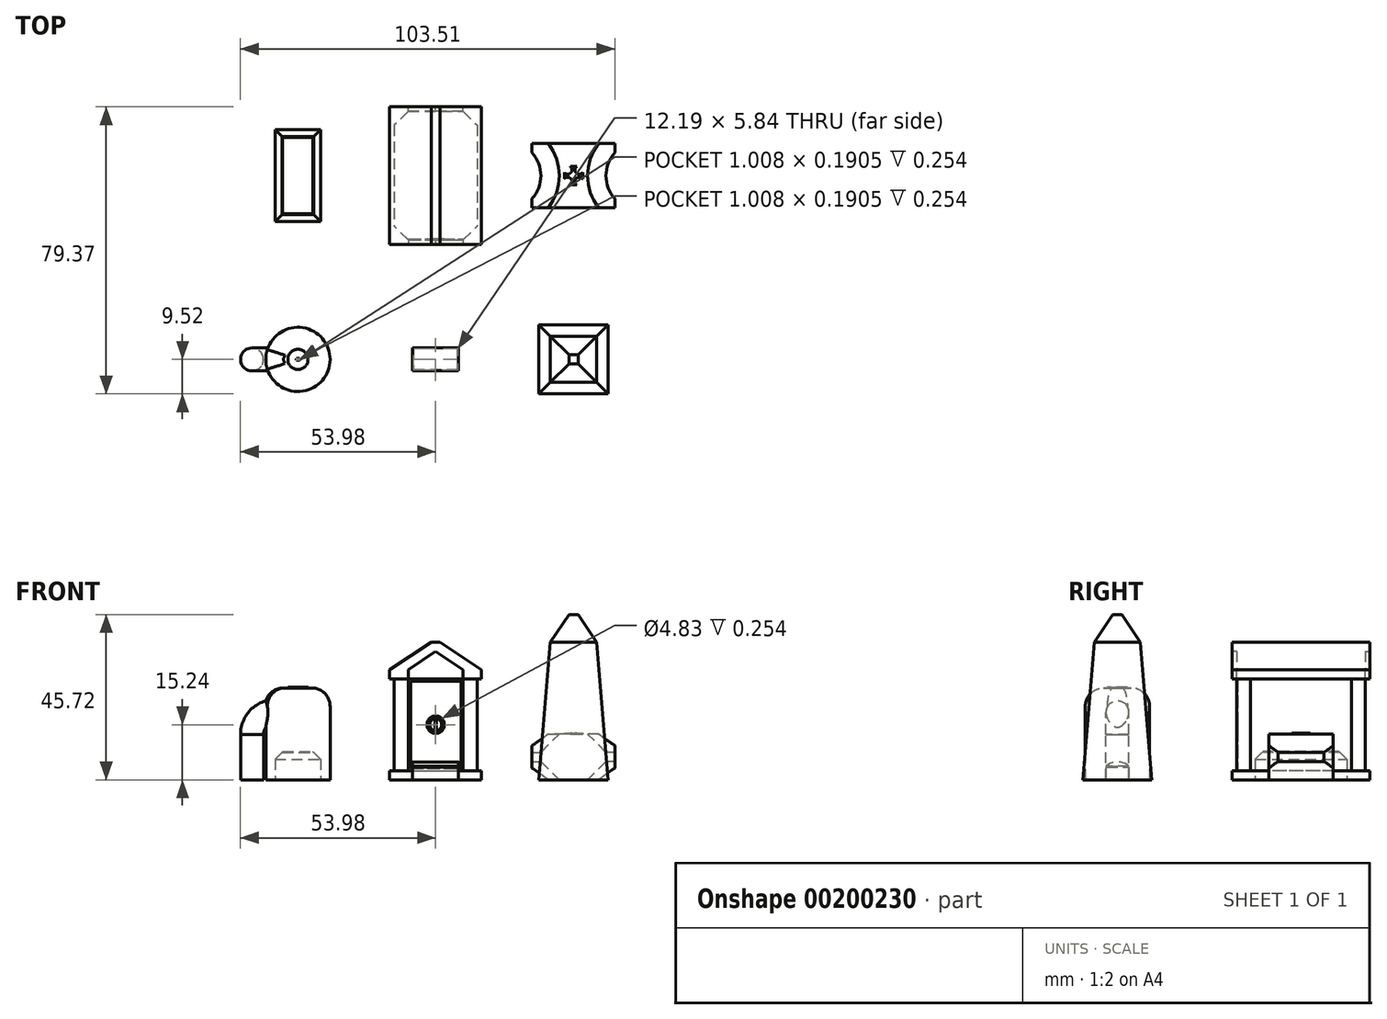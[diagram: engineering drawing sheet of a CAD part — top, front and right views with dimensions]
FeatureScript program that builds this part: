
annotation { "Feature Type Name" : "Feature", "Feature Type Description" : "" }
export const myFeature = defineFeature(function(context is Context, id is Id, definition is map)
    precondition{}
    {
        {
            var Q0;
            Q0=qCreatedBy(makeId("Top.planeOp"),FACE);
            var sketch = newSketch(context, id + "F0", { "sketchPlane" : qUnion([Q0])});
            skLineSegment(sketch, "E0", {"start": v(0, 0) * mm, "end": v(-38.1, 0) * mm, "construction": true});
            skLineSegment(sketch, "E1", {"start": v(0, 0) * mm, "end": v(38.1, 0) * mm, "construction": true});
            skLineSegment(sketch, "E2", {"start": v(0, 0) * mm, "end": v(0, 25.4) * mm, "construction": true});
            skLineSegment(sketch, "E3", {"start": v(-38.1, 0) * mm, "end": v(-38.1, 25.4) * mm, "construction": true});
            skLineSegment(sketch, "E4", {"start": v(38.1, 0) * mm, "end": v(38.1, 25.4) * mm, "construction": true});
            skLineSegment(sketch, "E5", {"start": v(-38.1, 0) * mm, "end": v(-38.1, -25.4) * mm, "construction": true});
            skLineSegment(sketch, "E6", {"start": v(0, 0) * mm, "end": v(0, -25.4) * mm, "construction": true});
            skLineSegment(sketch, "E7", {"start": v(38.1, 0) * mm, "end": v(38.1, -25.4) * mm, "construction": true});
            skSolve(sketch);
        }
        {
            var Q0;
            Q0=qCreatedBy(makeId("Top.planeOp"),FACE);
            var sketch = newSketch(context, id + "F1", { "sketchPlane" : qUnion([Q0])});
            skLineSegment(sketch, "E8.bottom", {"start": v(-44.45, 38.1) * mm, "end": v(-31.75, 38.1) * mm});
            skLineSegment(sketch, "E8.top", {"start": v(-44.45, 12.7) * mm, "end": v(-31.75, 12.7) * mm});
            skLineSegment(sketch, "E8.left", {"start": v(-44.45, 38.1) * mm, "end": v(-44.45, 12.7) * mm});
            skLineSegment(sketch, "E8.right", {"start": v(-31.75, 38.1) * mm, "end": v(-31.75, 12.7) * mm});
            skPoint(sketch, "E8.middle", {"position": v(-38.1, 25.4) * mm});
            skSolve(sketch);
        }
        {
            var Q0;
            Q0 = qSketchRegion(id + "F1", true);
            extrude(context, id + "F2", {"entities" : qUnion([Q0]), "depth" : 7.62 * mm});
        }
        {
            var Q0;
            Q0=makeQuery(id+"F2.opExtrude","CAP_FACE",FACE,{"disambiguationData":[OSD([sQuery(id+"F1.wireOp",EDGE,"E8.bottom"),sQuery(id+"F1.wireOp",EDGE,"E8.top"),sQuery(id+"F1.wireOp",EDGE,"E8.left"),sQuery(id+"F1.wireOp",EDGE,"E8.right")])],"isStart":false});
            chamfer(context, id + "F3", {"entities" : qUnion([Q0]), "width" : 1.9 * mm, "tangentPropagation" : true});
        }
        {
            var Q0;
            Q0=makeQuery(id+"F2.opExtrude","CAP_FACE",FACE,{"disambiguationData":[OSD([sQuery(id+"F1.wireOp",EDGE,"E8.bottom"),sQuery(id+"F1.wireOp",EDGE,"E8.top"),sQuery(id+"F1.wireOp",EDGE,"E8.left"),sQuery(id+"F1.wireOp",EDGE,"E8.right")])],"isStart":false});
            var sketch = newSketch(context, id + "F4", { "sketchPlane" : qUnion([Q0])});
            skLineSegment(sketch, "E9", {"start": v(-33.65, 25.4) * mm, "end": v(-38.1, 25.4) * mm, "construction": true});
            skPoint(sketch, "E9.endSnap0", {"position": v(-42.55, 25.4) * mm});
            skLineSegment(sketch, "E10.bottom", {"start": v(-42.3, 35.94) * mm, "end": v(-33.9, 35.94) * mm});
            skLineSegment(sketch, "E10.top", {"start": v(-42.3, 14.86) * mm, "end": v(-33.9, 14.86) * mm});
            skLineSegment(sketch, "E10.left", {"start": v(-42.3, 35.94) * mm, "end": v(-42.3, 14.86) * mm});
            skLineSegment(sketch, "E10.right", {"start": v(-33.9, 35.94) * mm, "end": v(-33.9, 14.86) * mm});
            skPoint(sketch, "E10.middle", {"position": v(-38.1, 25.4) * mm});
            skSolve(sketch);
        }
        {
            var Q0;
            Q0 = qSketchRegion(id + "F4", true);
            extrude(context, id + "F5", {"entities" : qUnion([Q0]), "operationType" : NewBodyOperationType.ADD, "depth" : 0.25 * mm});
        }
        {
            var Q0;
            Q0=qCreatedBy(makeId("Top.planeOp"),FACE);
            var sketch = newSketch(context, id + "F6", { "sketchPlane" : qUnion([Q0])});
            skLineSegment(sketch, "E11.bottom", {"start": v(-12.7, 44.45) * mm, "end": v(12.7, 44.45) * mm});
            skLineSegment(sketch, "E11.top", {"start": v(-12.7, 6.35) * mm, "end": v(12.7, 6.35) * mm});
            skLineSegment(sketch, "E11.left", {"start": v(-12.7, 44.45) * mm, "end": v(-12.7, 6.35) * mm});
            skLineSegment(sketch, "E11.right", {"start": v(12.7, 44.45) * mm, "end": v(12.7, 6.35) * mm});
            skPoint(sketch, "E11.middle", {"position": v(0, 25.4) * mm});
            skSolve(sketch);
        }
        {
            var Q0;
            Q0 = qSketchRegion(id + "F6", true);
            extrude(context, id + "F7", {"entities" : qUnion([Q0]), "depth" : 2.54 * mm});
        }
        {
            var Q0;
            Q0=makeQuery(id+"F7.opExtrude","CAP_FACE",FACE,{"disambiguationData":[OSD([sQuery(id+"F6.wireOp",EDGE,"E11.bottom"),sQuery(id+"F6.wireOp",EDGE,"E11.top"),sQuery(id+"F6.wireOp",EDGE,"E11.left"),sQuery(id+"F6.wireOp",EDGE,"E11.right")])],"isStart":false});
            var sketch = newSketch(context, id + "F8", { "sketchPlane" : qUnion([Q0])});
            skLineSegment(sketch, "E12.bottom", {"start": v(-11.43, 43.18) * mm, "end": v(11.43, 43.18) * mm});
            skLineSegment(sketch, "E12.top", {"start": v(-11.43, 7.62) * mm, "end": v(11.43, 7.62) * mm});
            skLineSegment(sketch, "E12.left", {"start": v(-11.43, 43.18) * mm, "end": v(-11.43, 7.62) * mm});
            skLineSegment(sketch, "E12.right", {"start": v(11.43, 43.18) * mm, "end": v(11.43, 7.62) * mm});
            skPoint(sketch, "E12.middle", {"position": v(0, 25.4) * mm});
            skSolve(sketch);
        }
        {
            var Q0;
            Q0 = qSketchRegion(id + "F8", true);
            extrude(context, id + "F9", {"entities" : qUnion([Q0]), "operationType" : NewBodyOperationType.ADD, "depth" : 25.4 * mm});
        }
        {
            var Q0;
            Q0=makeQuery(id+"F9.opExtrude","SWEPT_EDGE",EDGE,{"disambiguationData":[OSD([sQuery(id+"F8.wireOp",EDGE,"E12.top"),sQuery(id+"F8.wireOp",EDGE,"E12.left")])]});
            var Q1;
            Q1=makeQuery(id+"F9.opExtrude","SWEPT_EDGE",EDGE,{"disambiguationData":[OSD([sQuery(id+"F8.wireOp",EDGE,"E12.top"),sQuery(id+"F8.wireOp",EDGE,"E12.right")])]});
            var Q2;
            Q2=makeQuery(id+"F9.opExtrude","SWEPT_EDGE",EDGE,{"disambiguationData":[OSD([sQuery(id+"F8.wireOp",EDGE,"E12.bottom"),sQuery(id+"F8.wireOp",EDGE,"E12.right")])]});
            var Q3;
            Q3=makeQuery(id+"F9.opExtrude","SWEPT_EDGE",EDGE,{"disambiguationData":[OSD([sQuery(id+"F8.wireOp",EDGE,"E12.bottom"),sQuery(id+"F8.wireOp",EDGE,"E12.left")])]});
            chamfer(context, id + "F10", {"entities" : qUnion([Q0, Q1, Q2, Q3]), "width" : 3.8 * mm, "tangentPropagation" : true});
        }
        {
            var Q0;
            Q0=makeQuery(id+"F9.opExtrude","CAP_FACE",FACE,{"disambiguationData":[OSD([sQuery(id+"F8.wireOp",EDGE,"E12.bottom"),sQuery(id+"F8.wireOp",EDGE,"E12.top"),sQuery(id+"F8.wireOp",EDGE,"E12.left"),sQuery(id+"F8.wireOp",EDGE,"E12.right")])],"isStart":false});
            var sketch = newSketch(context, id + "F11", { "sketchPlane" : qUnion([Q0])});
            skLineSegment(sketch, "E13.bottom", {"start": v(-12.7, 44.45) * mm, "end": v(12.7, 44.45) * mm});
            skLineSegment(sketch, "E13.top", {"start": v(-12.7, 6.35) * mm, "end": v(12.7, 6.35) * mm});
            skLineSegment(sketch, "E13.left", {"start": v(-12.7, 44.45) * mm, "end": v(-12.7, 6.35) * mm});
            skLineSegment(sketch, "E13.right", {"start": v(12.7, 44.45) * mm, "end": v(12.7, 6.35) * mm});
            skPoint(sketch, "E13.middle", {"position": v(0, 25.4) * mm});
            skSolve(sketch);
        }
        {
            var Q0;
            {var subQ3=sQuery(id+"F8.wireOp",EDGE,"E12.bottom");Q0=makeQuery(id+"F11.imprint","IMPRINT",FACE,{"disambiguationData":[TD([[makeQuery(id+"F11.imprint","IMPRINT",EDGE,{"derivedFrom":makeQuery(id+"F9.opExtrude","CAP_EDGE",EDGE,{"disambiguationData":[OSD([subQ3])],"isStart":false})}),-1.0]])]});}
            cPlane(context, id + "F12", {"entities" : qUnion([Q0]), "cplaneType" : CPlaneType.OFFSET, "offset" : 10.16 * mm, "width" : 152.4 * mm, "height" : 152.4 * mm});
        }
        {
            var Q0;
            Q0=qCreatedBy(id+"F12.planeOp",FACE);
            var sketch = newSketch(context, id + "F13", { "sketchPlane" : qUnion([Q0])});
            skLineSegment(sketch, "E14.bottom", {"start": v(-1.27, 44.45) * mm, "end": v(1.27, 44.45) * mm});
            skLineSegment(sketch, "E14.top", {"start": v(-1.27, 6.35) * mm, "end": v(1.27, 6.35) * mm});
            skLineSegment(sketch, "E14.left", {"start": v(-1.27, 44.45) * mm, "end": v(-1.27, 6.35) * mm});
            skLineSegment(sketch, "E14.right", {"start": v(1.27, 44.45) * mm, "end": v(1.27, 6.35) * mm});
            skPoint(sketch, "E14.middle", {"position": v(0, 25.4) * mm});
            skSolve(sketch);
        }
        {
            var Q0;
            Q0=qCreatedBy(makeId("Front.planeOp"),FACE);
            cPlane(context, id + "F14", {"entities" : qUnion([Q0]), "cplaneType" : CPlaneType.OFFSET, "offset" : 6.35 * mm, "oppositeDirection" : true, "width" : 152.4 * mm, "height" : 152.4 * mm});
        }
        {
            var Q0;
            Q0=qCreatedBy(id+"F14.planeOp",FACE);
            var sketch = newSketch(context, id + "F15", { "sketchPlane" : qUnion([Q0])});
            skLineSegment(sketch, "E15", {"start": v(-12.7, 27.94) * mm, "end": v(-12.7, 30.48) * mm});
            skLineSegment(sketch, "E16", {"start": v(-12.7, 30.48) * mm, "end": v(-1.27, 38.1) * mm});
            skLineSegment(sketch, "E17", {"start": v(-1.27, 38.1) * mm, "end": v(1.27, 38.1) * mm});
            skLineSegment(sketch, "E18", {"start": v(1.27, 38.1) * mm, "end": v(12.7, 30.48) * mm});
            skLineSegment(sketch, "E19", {"start": v(12.7, 30.48) * mm, "end": v(12.7, 27.94) * mm});
            skLineSegment(sketch, "E20", {"start": v(-12.7, 27.94) * mm, "end": v(12.7, 27.94) * mm});
            skSolve(sketch);
        }
        {
            var Q0;
            Q0 = qSketchRegion(id + "F15", true);
            extrude(context, id + "F16", {"entities" : qUnion([Q0]), "oppositeDirection" : true, "depth" : 38.1 * mm});
        }
        {
            var Q0;
            Q0=makeQuery(id+"F16.opExtrude","CAP_FACE",FACE,{"disambiguationData":[OSD([sQuery(id+"F15.wireOp",EDGE,"E15"),sQuery(id+"F15.wireOp",EDGE,"E16"),sQuery(id+"F15.wireOp",EDGE,"E17"),sQuery(id+"F15.wireOp",EDGE,"E18"),sQuery(id+"F15.wireOp",EDGE,"E19"),sQuery(id+"F15.wireOp",EDGE,"E20")])],"isStart":true});
            var sketch = newSketch(context, id + "F17", { "sketchPlane" : qUnion([Q0])});
            skLineSegment(sketch, "E21", {"start": v(-7.62, 27.94) * mm, "end": v(-7.62, 30.48) * mm});
            skLineSegment(sketch, "E22", {"start": v(-7.62, 30.48) * mm, "end": v(0, 35.56) * mm});
            skLineSegment(sketch, "E23", {"start": v(0, 35.56) * mm, "end": v(7.62, 30.48) * mm});
            skLineSegment(sketch, "E24", {"start": v(7.62, 30.48) * mm, "end": v(7.62, 27.94) * mm});
            skLineSegment(sketch, "E25", {"start": v(-7.62, 27.94) * mm, "end": v(7.62, 27.94) * mm});
            skSolve(sketch);
        }
        {
            var Q0;
            Q0 = qSketchRegion(id + "F17", true);
            extrude(context, id + "F18", {"entities" : qUnion([Q0]), "operationType" : NewBodyOperationType.REMOVE, "oppositeDirection" : true, "depth" : 1.27 * mm});
        }
        {
            var Q0;
            Q0=makeQuery(id+"F16.opExtrude","CAP_FACE",FACE,{"disambiguationData":[OSD([sQuery(id+"F15.wireOp",EDGE,"E15"),sQuery(id+"F15.wireOp",EDGE,"E16"),sQuery(id+"F15.wireOp",EDGE,"E17"),sQuery(id+"F15.wireOp",EDGE,"E18"),sQuery(id+"F15.wireOp",EDGE,"E19"),sQuery(id+"F15.wireOp",EDGE,"E20")])],"isStart":false});
            var sketch = newSketch(context, id + "F19", { "sketchPlane" : qUnion([Q0])});
            skLineSegment(sketch, "E26", {"start": v(-7.62, 27.94) * mm, "end": v(-7.62, 30.48) * mm});
            skLineSegment(sketch, "E27", {"start": v(-7.62, 30.48) * mm, "end": v(0, 35.56) * mm});
            skLineSegment(sketch, "E28", {"start": v(0, 35.56) * mm, "end": v(7.62, 30.48) * mm});
            skLineSegment(sketch, "E29", {"start": v(7.62, 30.48) * mm, "end": v(7.62, 27.94) * mm});
            skLineSegment(sketch, "E30", {"start": v(-7.62, 27.94) * mm, "end": v(7.62, 27.94) * mm});
            skSolve(sketch);
        }
        {
            var Q0;
            Q0 = qSketchRegion(id + "F19", true);
            extrude(context, id + "F20", {"entities" : qUnion([Q0]), "operationType" : NewBodyOperationType.REMOVE, "oppositeDirection" : true, "depth" : 1.27 * mm});
        }
        {
            var Q0;
            Q0=makeQuery(id+"F9.opExtrude","SWEPT_FACE",FACE,{"disambiguationData":[OSD([sQuery(id+"F8.wireOp",EDGE,"E12.top")])]});
            var sketch = newSketch(context, id + "F21", { "sketchPlane" : qUnion([Q0])});
            skLineSegment(sketch, "E31.bottom", {"start": v(-7.62, 2.54) * mm, "end": v(7.62, 2.54) * mm});
            skLineSegment(sketch, "E31.top", {"start": v(-7.62, 27.94) * mm, "end": v(7.62, 27.94) * mm});
            skLineSegment(sketch, "E31.left", {"start": v(-7.62, 2.54) * mm, "end": v(-7.62, 27.94) * mm});
            skLineSegment(sketch, "E31.right", {"start": v(7.62, 2.54) * mm, "end": v(7.62, 27.94) * mm});
            skLineSegment(sketch, "E32.bottom", {"start": v(-6.99, 27.3) * mm, "end": v(6.98, 27.3) * mm});
            skLineSegment(sketch, "E32.top", {"start": v(-6.98, 3.18) * mm, "end": v(6.99, 3.18) * mm});
            skLineSegment(sketch, "E32.left", {"start": v(-6.99, 27.3) * mm, "end": v(-6.98, 3.17) * mm});
            skLineSegment(sketch, "E32.right", {"start": v(6.98, 27.3) * mm, "end": v(6.99, 3.18) * mm});
            skPoint(sketch, "E32.middle", {"position": v(0, 15.24) * mm});
            skSolve(sketch);
        }
        {
            var Q0;
            Q0 = qSketchRegion(id + "F21", true);
            extrude(context, id + "F22", {"entities" : qUnion([Q0]), "operationType" : NewBodyOperationType.REMOVE, "oppositeDirection" : true, "depth" : 0.25 * mm});
        }
        {
            var Q0;
            Q0=makeQuery(id+"F9.opExtrude","SWEPT_FACE",FACE,{"disambiguationData":[OSD([sQuery(id+"F8.wireOp",EDGE,"E12.top")])]});
            var sketch = newSketch(context, id + "F23", { "sketchPlane" : qUnion([Q0])});
            skCircle(sketch, "E33", {"center": v(0, 15.24) * mm, "radius": 2.03 * mm});
            skLineSegment(sketch, "E34", {"start": v(0, 15.24) * mm, "end": v(-0.25, 15.24) * mm, "construction": true});
            skLineSegment(sketch, "E35", {"start": v(0, 15.24) * mm, "end": v(0.25, 15.24) * mm, "construction": true});
            skLineSegment(sketch, "E36", {"start": v(-0.25, 15.24) * mm, "end": v(-0.25, 16.87) * mm});
            skLineSegment(sketch, "E37", {"start": v(-0.25, 15.24) * mm, "end": v(-0.25, 13.6) * mm});
            skLineSegment(sketch, "E38", {"start": v(0.25, 15.24) * mm, "end": v(0.25, 16.87) * mm});
            skLineSegment(sketch, "E39", {"start": v(0.25, 15.24) * mm, "end": v(0.25, 13.6) * mm});
            skArc(sketch, "E40", {"start": v(0.25, 16.87) * mm, "mid": v(1.65, 15.24) * mm, "end": v(0.25, 13.6) * mm});
            skArc(sketch, "E41", {"start": v(-0.25, 16.87) * mm, "mid": v(-1.65, 15.24) * mm, "end": v(-0.25, 13.6) * mm});
            skCircle(sketch, "E42", {"center": v(0, 15.24) * mm, "radius": 2.41 * mm});
            skSolve(sketch);
        }
        {
            var Q0;
            Q0 = qSketchRegion(id + "F23", true);
            var Q1;
            Q1=makeQuery(id+"F23.imprint","IMPRINT",FACE,{"disambiguationData":[TD([[makeQuery(id+"F23.imprint","IMPRINT",EDGE,{"derivedFrom":sQuery(id+"F23.wireOp",EDGE,"E36")}),1.0]])]});
            var Q2;
            Q2=makeQuery(id+"F23.imprint","IMPRINT",FACE,{"disambiguationData":[TD([[makeQuery(id+"F23.imprint","IMPRINT",EDGE,{"derivedFrom":sQuery(id+"F23.wireOp",EDGE,"E38")}),-1.0]])]});
            extrude(context, id + "F24", {"entities" : qUnion([Q0, Q1, Q2]), "operationType" : NewBodyOperationType.REMOVE, "oppositeDirection" : true, "depth" : 0.25 * mm});
        }
        {
            var Q0;
            Q0=qCreatedBy(makeId("Top.planeOp"),FACE);
            var sketch = newSketch(context, id + "F25", { "sketchPlane" : qUnion([Q0])});
            skLineSegment(sketch, "E43", {"start": v(38.1, 25.4) * mm, "end": v(38.1, 16.51) * mm, "construction": true});
            skLineSegment(sketch, "E44", {"start": v(38.1, 25.4) * mm, "end": v(38.1, 34.3) * mm, "construction": true});
            skLineSegment(sketch, "E45", {"start": v(38.1, 34.3) * mm, "end": v(26.67, 34.3) * mm});
            skLineSegment(sketch, "E46", {"start": v(38.1, 16.51) * mm, "end": v(26.67, 16.51) * mm});
            skLineSegment(sketch, "E47", {"start": v(26.67, 16.51) * mm, "end": v(26.67, 19.05) * mm});
            skLineSegment(sketch, "E48", {"start": v(26.67, 34.3) * mm, "end": v(26.67, 31.75) * mm});
            skArc(sketch, "E49", {"start": v(26.67, 19.05) * mm, "mid": v(29.1, 25.4) * mm, "end": v(26.67, 31.75) * mm});
            skLineSegment(sketch, "E50.MirrorCS", {"start": v(49.53, 34.3) * mm, "end": v(49.53, 31.75) * mm});
            skLineSegment(sketch, "E51.MirrorCS", {"start": v(38.1, 34.3) * mm, "end": v(49.53, 34.3) * mm});
            skArc(sketch, "E52.MirrorCS", {"start": v(49.53, 19.05) * mm, "mid": v(47.1, 25.4) * mm, "end": v(49.53, 31.75) * mm});
            skLineSegment(sketch, "E53.MirrorCS", {"start": v(38.1, 16.51) * mm, "end": v(49.53, 16.51) * mm});
            skLineSegment(sketch, "E54.MirrorCS", {"start": v(49.53, 16.51) * mm, "end": v(49.53, 19.05) * mm});
            skSolve(sketch);
        }
        {
            var Q0;
            Q0 = qSketchRegion(id + "F25", true);
            extrude(context, id + "F26", {"entities" : qUnion([Q0]), "depth" : 12.7 * mm});
        }
        {
            var Q0;
            Q0=makeQuery(id+"F26.opExtrude","CAP_EDGE",EDGE,{"disambiguationData":[OSD([sQuery(id+"F25.wireOp",EDGE,"E49")])],"isStart":false});
            var Q1;
            Q1=makeQuery(id+"F26.opExtrude","CAP_EDGE",EDGE,{"disambiguationData":[OSD([sQuery(id+"F25.wireOp",EDGE,"E52.MirrorCS")])],"isStart":false});
            var Q2;
            Q2=makeQuery(id+"F26.opExtrude","CAP_EDGE",EDGE,{"disambiguationData":[OSD([sQuery(id+"F25.wireOp",EDGE,"E52.MirrorCS")])],"isStart":true});
            var Q3;
            Q3=makeQuery(id+"F26.opExtrude","CAP_EDGE",EDGE,{"disambiguationData":[OSD([sQuery(id+"F25.wireOp",EDGE,"E49")])],"isStart":true});
            chamfer(context, id + "F27", {"entities" : qUnion([Q0, Q1, Q2, Q3]), "width" : 5.08 * mm, "tangentPropagation" : true});
        }
        {
            var Q0;
            Q0=makeQuery(id+"F26.opExtrude","CAP_FACE",FACE,{"disambiguationData":[OSD([sQuery(id+"F25.wireOp",EDGE,"E45"),sQuery(id+"F25.wireOp",EDGE,"E46"),sQuery(id+"F25.wireOp",EDGE,"E47"),sQuery(id+"F25.wireOp",EDGE,"E48"),sQuery(id+"F25.wireOp",EDGE,"E49"),sQuery(id+"F25.wireOp",EDGE,"E50.MirrorCS"),sQuery(id+"F25.wireOp",EDGE,"E51.MirrorCS"),sQuery(id+"F25.wireOp",EDGE,"E52.MirrorCS"),sQuery(id+"F25.wireOp",EDGE,"E53.MirrorCS"),sQuery(id+"F25.wireOp",EDGE,"E54.MirrorCS")])],"isStart":false});
            var sketch = newSketch(context, id + "F28", { "sketchPlane" : qUnion([Q0])});
            skLineSegment(sketch, "E55", {"start": v(38.1, 25.4) * mm, "end": v(35.56, 25.4) * mm, "construction": true});
            skLineSegment(sketch, "E56", {"start": v(38.1, 25.4) * mm, "end": v(38.1, 27.94) * mm, "construction": true});
            skLineSegment(sketch, "E57", {"start": v(38.1, 25.4) * mm, "end": v(40.64, 25.4) * mm, "construction": true});
            skLineSegment(sketch, "E58", {"start": v(38.1, 25.4) * mm, "end": v(38.1, 22.86) * mm, "construction": true});
            skLineSegment(sketch, "E59", {"start": v(37.21, 27.94) * mm, "end": v(38.99, 27.94) * mm});
            skLineSegment(sketch, "E60.MirrorCS", {"start": v(37.21, 22.86) * mm, "end": v(38.99, 22.86) * mm});
            skLineSegment(sketch, "E61", {"start": v(35.56, 26.29) * mm, "end": v(35.56, 24.51) * mm});
            skLineSegment(sketch, "E62.MirrorCS", {"start": v(40.64, 26.29) * mm, "end": v(40.64, 24.51) * mm});
            skLineSegment(sketch, "E63.bottom", {"start": v(37.34, 26.16) * mm, "end": v(38.86, 26.16) * mm, "construction": true});
            skLineSegment(sketch, "E63.top", {"start": v(37.34, 24.64) * mm, "end": v(38.86, 24.64) * mm, "construction": true});
            skLineSegment(sketch, "E63.left", {"start": v(37.34, 26.16) * mm, "end": v(37.34, 24.64) * mm, "construction": true});
            skLineSegment(sketch, "E63.right", {"start": v(38.86, 26.16) * mm, "end": v(38.86, 24.64) * mm, "construction": true});
            skPoint(sketch, "E63.middle", {"position": v(38.1, 25.4) * mm});
            skArc(sketch, "E64", {"start": v(35.56, 26.29) * mm, "mid": v(37.34, 26.16) * mm, "end": v(37.21, 27.94) * mm});
            skArc(sketch, "E65", {"start": v(38.99, 27.94) * mm, "mid": v(38.86, 26.16) * mm, "end": v(40.64, 26.29) * mm});
            skArc(sketch, "E66", {"start": v(40.64, 24.51) * mm, "mid": v(38.86, 24.64) * mm, "end": v(38.99, 22.86) * mm});
            skArc(sketch, "E67", {"start": v(37.21, 22.86) * mm, "mid": v(37.34, 24.64) * mm, "end": v(35.56, 24.51) * mm});
            skSolve(sketch);
        }
        {
            var Q0;
            Q0 = qSketchRegion(id + "F28", true);
            extrude(context, id + "F29", {"entities" : qUnion([Q0]), "operationType" : NewBodyOperationType.ADD, "depth" : 0.25 * mm});
        }
        {
            var Q0;
            Q0=qCreatedBy(makeId("Top.planeOp"),FACE);
            var sketch = newSketch(context, id + "F30", { "sketchPlane" : qUnion([Q0])});
            skLineSegment(sketch, "E68.bottom", {"start": v(28.58, -15.88) * mm, "end": v(47.63, -15.88) * mm});
            skLineSegment(sketch, "E68.top", {"start": v(28.57, -34.92) * mm, "end": v(47.63, -34.92) * mm});
            skLineSegment(sketch, "E68.left", {"start": v(28.58, -15.88) * mm, "end": v(28.57, -34.92) * mm});
            skLineSegment(sketch, "E68.right", {"start": v(47.63, -15.88) * mm, "end": v(47.63, -34.92) * mm});
            skPoint(sketch, "E68.middle", {"position": v(38.1, -25.4) * mm});
            skSolve(sketch);
        }
        {
            var Q0;
            Q0=makeQuery(id+"F30.imprint","IMPRINT",FACE,{"disambiguationData":[TD([[makeQuery(id+"F30.imprint","IMPRINT",EDGE,{"derivedFrom":sQuery(id+"F30.wireOp",EDGE,"E68.bottom")}),-1.0]])]});
            cPlane(context, id + "F31", {"entities" : qUnion([Q0]), "cplaneType" : CPlaneType.OFFSET, "offset" : 38.1 * mm, "width" : 152.4 * mm, "height" : 152.4 * mm});
        }
        {
            var Q0;
            Q0=qCreatedBy(id+"F31.planeOp",FACE);
            var sketch = newSketch(context, id + "F32", { "sketchPlane" : qUnion([Q0])});
            skLineSegment(sketch, "E69.bottom", {"start": v(31.75, -19.05) * mm, "end": v(44.45, -19.05) * mm});
            skLineSegment(sketch, "E69.top", {"start": v(31.75, -31.75) * mm, "end": v(44.45, -31.75) * mm});
            skLineSegment(sketch, "E69.left", {"start": v(31.75, -19.05) * mm, "end": v(31.75, -31.75) * mm});
            skLineSegment(sketch, "E69.right", {"start": v(44.45, -19.05) * mm, "end": v(44.45, -31.75) * mm});
            skPoint(sketch, "E69.middle", {"position": v(38.1, -25.4) * mm});
            skSolve(sketch);
        }
        {
            var Q0;
            Q0=qCreatedBy(id+"F31.planeOp",FACE);
            cPlane(context, id + "F33", {"entities" : qUnion([Q0]), "cplaneType" : CPlaneType.OFFSET, "offset" : 7.62 * mm, "width" : 152.4 * mm, "height" : 152.4 * mm});
        }
        {
            var Q0;
            Q0=qCreatedBy(id+"F33.planeOp",FACE);
            var sketch = newSketch(context, id + "F34", { "sketchPlane" : qUnion([Q0])});
            skLineSegment(sketch, "E70.bottom", {"start": v(36.83, -24.13) * mm, "end": v(39.37, -24.13) * mm});
            skLineSegment(sketch, "E70.top", {"start": v(36.83, -26.67) * mm, "end": v(39.37, -26.67) * mm});
            skLineSegment(sketch, "E70.left", {"start": v(36.83, -24.13) * mm, "end": v(36.83, -26.67) * mm});
            skLineSegment(sketch, "E70.right", {"start": v(39.37, -24.13) * mm, "end": v(39.37, -26.67) * mm});
            skPoint(sketch, "E70.middle", {"position": v(38.1, -25.4) * mm});
            skSolve(sketch);
        }
        {
            var Q0;
            Q0 = qSketchRegion(id + "F30", true);
            var Q1;
            Q1 = qSketchRegion(id + "F32", true);
            loft(context, id + "F35", {"sheetProfilesArray" : [{ "sheetProfileEntities" : qUnion([Q0]) }, { "sheetProfileEntities" : qUnion([Q1]) }]});
        }
        {
            var Q1;
            Q1 = qSketchRegion(id + "F32", true);
            var Q2;
            Q2 = qSketchRegion(id + "F34", true);
            loft(context, id + "F36", {"operationType" : NewBodyOperationType.ADD, "sheetProfilesArray" : [{ "sheetProfileEntities" : qUnion([Q1]) }, { "sheetProfileEntities" : qUnion([Q2]) }]});
        }
        {
            var Q0;
            Q0=qCreatedBy(makeId("Right.planeOp"),FACE);
            cPlane(context, id + "F37", {"entities" : qUnion([Q0]), "cplaneType" : CPlaneType.OFFSET, "offset" : 6.35 * mm, "oppositeDirection" : true, "width" : 152.4 * mm, "height" : 152.4 * mm});
        }
        {
            var Q0;
            Q0=qCreatedBy(id+"F37.planeOp",FACE);
            var sketch = newSketch(context, id + "F38", { "sketchPlane" : qUnion([Q0])});
            skLineSegment(sketch, "E71", {"start": v(0, 0) * mm, "end": v(-25.4, 0) * mm, "construction": true});
            skLineSegment(sketch, "E72", {"start": v(-22.23, 0) * mm, "end": v(-28.57, 0) * mm});
            skArc(sketch, "E73", {"start": v(-22.23, 3.8) * mm, "mid": v(-25.4, 4.96) * mm, "end": v(-28.58, 3.8) * mm});
            skLineSegment(sketch, "E74", {"start": v(-28.58, 3.8) * mm, "end": v(-28.32, 3.8) * mm});
            skLineSegment(sketch, "E75", {"start": v(-28.32, 3.8) * mm, "end": v(-28.32, 3.56) * mm});
            skLineSegment(sketch, "E76", {"start": v(-28.32, 3.56) * mm, "end": v(-28.58, 3.56) * mm});
            skLineSegment(sketch, "E77", {"start": v(-28.57, 3.56) * mm, "end": v(-28.57, 0) * mm});
            skLineSegment(sketch, "E78", {"start": v(-25.4, 0) * mm, "end": v(-25.4, 4.96) * mm, "construction": true});
            skLineSegment(sketch, "E79.MirrorCS", {"start": v(-22.48, 3.8) * mm, "end": v(-22.48, 3.56) * mm});
            skLineSegment(sketch, "E80.MirrorCS", {"start": v(-22.22, 3.8) * mm, "end": v(-22.48, 3.8) * mm});
            skLineSegment(sketch, "E81.MirrorCS", {"start": v(-22.48, 3.56) * mm, "end": v(-22.22, 3.56) * mm});
            skLineSegment(sketch, "E82.MirrorCS", {"start": v(-22.23, 3.56) * mm, "end": v(-22.23, 0) * mm});
            skSolve(sketch);
        }
        {
            var Q0;
            Q0 = qSketchRegion(id + "F38", true);
            extrude(context, id + "F39", {"entities" : qUnion([Q0]), "depth" : 12.7 * mm});
        }
        {
            var Q0;
            Q0=makeQuery(id+"F39.opExtrude","CAP_FACE",FACE,{"disambiguationData":[OSD([sQuery(id+"F38.wireOp",EDGE,"E72"),sQuery(id+"F38.wireOp",EDGE,"E73"),sQuery(id+"F38.wireOp",EDGE,"E74"),sQuery(id+"F38.wireOp",EDGE,"E75"),sQuery(id+"F38.wireOp",EDGE,"E76"),sQuery(id+"F38.wireOp",EDGE,"E77"),sQuery(id+"F38.wireOp",EDGE,"E79.MirrorCS"),sQuery(id+"F38.wireOp",EDGE,"E80.MirrorCS"),sQuery(id+"F38.wireOp",EDGE,"E81.MirrorCS"),sQuery(id+"F38.wireOp",EDGE,"E82.MirrorCS")])],"isStart":true});
            var sketch = newSketch(context, id + "F40", { "sketchPlane" : qUnion([Q0])});
            skLineSegment(sketch, "E83.bottom", {"start": v(22.48, 3.8) * mm, "end": v(28.32, 3.8) * mm});
            skLineSegment(sketch, "E83.top", {"start": v(22.48, 3.56) * mm, "end": v(28.32, 3.56) * mm});
            skLineSegment(sketch, "E83.left", {"start": v(22.48, 3.8) * mm, "end": v(22.48, 3.56) * mm});
            skLineSegment(sketch, "E83.right", {"start": v(28.32, 3.8) * mm, "end": v(28.32, 3.56) * mm});
            skSolve(sketch);
        }
        {
            var Q0;
            Q0 = qSketchRegion(id + "F40", true);
            extrude(context, id + "F41", {"entities" : qUnion([Q0]), "operationType" : NewBodyOperationType.REMOVE, "oppositeDirection" : true, "depth" : 0.25 * mm});
        }
        {
            var Q0;
            Q0=makeQuery(id+"F39.opExtrude","CAP_FACE",FACE,{"disambiguationData":[OSD([sQuery(id+"F38.wireOp",EDGE,"E72"),sQuery(id+"F38.wireOp",EDGE,"E73"),sQuery(id+"F38.wireOp",EDGE,"E74"),sQuery(id+"F38.wireOp",EDGE,"E75"),sQuery(id+"F38.wireOp",EDGE,"E76"),sQuery(id+"F38.wireOp",EDGE,"E77"),sQuery(id+"F38.wireOp",EDGE,"E79.MirrorCS"),sQuery(id+"F38.wireOp",EDGE,"E80.MirrorCS"),sQuery(id+"F38.wireOp",EDGE,"E81.MirrorCS"),sQuery(id+"F38.wireOp",EDGE,"E82.MirrorCS")])],"isStart":false});
            var sketch = newSketch(context, id + "F42", { "sketchPlane" : qUnion([Q0])});
            skLineSegment(sketch, "E84.bottom", {"start": v(-28.32, 3.8) * mm, "end": v(-22.48, 3.8) * mm});
            skLineSegment(sketch, "E84.top", {"start": v(-28.32, 3.56) * mm, "end": v(-22.48, 3.56) * mm});
            skLineSegment(sketch, "E84.left", {"start": v(-28.32, 3.8) * mm, "end": v(-28.32, 3.56) * mm});
            skLineSegment(sketch, "E84.right", {"start": v(-22.48, 3.8) * mm, "end": v(-22.48, 3.56) * mm});
            skSolve(sketch);
        }
        {
            var Q0;
            Q0 = qSketchRegion(id + "F42", true);
            extrude(context, id + "F43", {"entities" : qUnion([Q0]), "operationType" : NewBodyOperationType.REMOVE, "oppositeDirection" : true, "depth" : 0.25 * mm});
        }
        {
            var Q0;
            Q0=qCreatedBy(makeId("Top.planeOp"),FACE);
            var sketch = newSketch(context, id + "F44", { "sketchPlane" : qUnion([Q0])});
            skCircle(sketch, "E85", {"center": v(-38.1, -25.4) * mm, "radius": 8.9 * mm});
            skSolve(sketch);
        }
        {
            var Q0;
            Q0 = qSketchRegion(id + "F44", true);
            extrude(context, id + "F45", {"entities" : qUnion([Q0]), "depth" : 25.4 * mm});
        }
        {
            var Q0;
            Q0=qCreatedBy(makeId("Front.planeOp"),FACE);
            cPlane(context, id + "F46", {"entities" : qUnion([Q0]), "cplaneType" : CPlaneType.OFFSET, "offset" : 25.4 * mm, "width" : 152.4 * mm, "height" : 152.4 * mm});
        }
        {
            var Q0;
            Q0=qCreatedBy(id+"F46.planeOp",FACE);
            var sketch = newSketch(context, id + "F47", { "sketchPlane" : qUnion([Q0])});
            skPoint(sketch, "E86", {"position": v(-38.1, 0) * mm});
            skLineSegment(sketch, "E87", {"start": v(-38.1, 0) * mm, "end": v(-50.8, 0) * mm, "construction": true});
            skLineSegment(sketch, "E88", {"start": v(-50.8, 0) * mm, "end": v(-50.8, 12.7) * mm});
            skArc(sketch, "E89", {"start": v(-50.8, 12.7) * mm, "mid": v(-48.91, 17.14) * mm, "end": v(-44.45, 18.97) * mm});
            skLineSegment(sketch, "E90", {"start": v(-44.45, 18.97) * mm, "end": v(-38.1, 18.97) * mm});
            skSolve(sketch);
        }
        {
            var Q0;
            Q0=qCreatedBy(makeId("Top.planeOp"),FACE);
            var sketch = newSketch(context, id + "F48", { "sketchPlane" : qUnion([Q0])});
            skCircle(sketch, "E91", {"center": v(-50.8, -25.4) * mm, "radius": 3.18 * mm});
            skSolve(sketch);
        }
        {
            var Q0;
            Q0 = qSketchRegion(id + "F48", true);
            var Q1;
            Q1=sQuery(id+"F47.wireOp",EDGE,"E88");
            var Q2;
            Q2=sQuery(id+"F47.wireOp",EDGE,"E89");
            sweep(context, id + "F49", {"operationType" : NewBodyOperationType.ADD, "profiles" : qUnion([Q0]), "path" : qUnion([Q1, Q2])});
        }
        {
            var Q0;
            Q0=makeQuery(id+"F45.opExtrude","CAP_EDGE",EDGE,{"disambiguationData":[OSD([sQuery(id+"F44.wireOp",EDGE,"E85")])],"isStart":false});
            fillet(context, id + "F50", {"entities" : qUnion([Q0]), "radius" : 5.08 * mm, "tangentPropagation" : true, "allowEdgeOverflow" : false});
        }
        {
            var Q0;
            Q0=makeQuery(id+"F45.opExtrude","CAP_FACE",FACE,{"disambiguationData":[OSD([sQuery(id+"F44.wireOp",EDGE,"E85")])],"isStart":false});
            var sketch = newSketch(context, id + "F51", { "sketchPlane" : qUnion([Q0])});
            skCircle(sketch, "E92", {"center": v(-38.1, -25.4) * mm, "radius": 2.8 * mm});
            skLineSegment(sketch, "E93", {"start": v(-38.1, -25.15) * mm, "end": v(-38.1, -25.65) * mm, "construction": true});
            skLineSegment(sketch, "E94.bottom", {"start": v(-38.6, -25.34) * mm, "end": v(-37.6, -25.34) * mm});
            skLineSegment(sketch, "E94.top", {"start": v(-38.6, -25.46) * mm, "end": v(-37.6, -25.46) * mm});
            skLineSegment(sketch, "E95", {"start": v(-38.6, -25.34) * mm, "end": v(-38.6, -25.15) * mm});
            skLineSegment(sketch, "E96", {"start": v(-38.6, -25.15) * mm, "end": v(-37.6, -25.15) * mm});
            skLineSegment(sketch, "E97", {"start": v(-37.6, -25.15) * mm, "end": v(-37.6, -25.34) * mm});
            skLineSegment(sketch, "E98", {"start": v(-37.6, -25.4) * mm, "end": v(-38.6, -25.4) * mm, "construction": true});
            skLineSegment(sketch, "E99.MirrorCS", {"start": v(-38.6, -25.46) * mm, "end": v(-38.6, -25.65) * mm});
            skLineSegment(sketch, "E100.MirrorCS", {"start": v(-38.6, -25.65) * mm, "end": v(-37.6, -25.65) * mm});
            skLineSegment(sketch, "E101.MirrorCS", {"start": v(-37.6, -25.65) * mm, "end": v(-37.6, -25.46) * mm});
            skSolve(sketch);
        }
        {
            var Q0;
            Q0=makeQuery(id+"F51.imprint","IMPRINT",FACE,{"disambiguationData":[TD([[makeQuery(id+"F51.imprint","IMPRINT",EDGE,{"derivedFrom":sQuery(id+"F51.wireOp",EDGE,"E92")}),1.0]])]});
            extrude(context, id + "F52", {"entities" : qUnion([Q0]), "operationType" : NewBodyOperationType.ADD, "depth" : 0.25 * mm});
        }
    });
